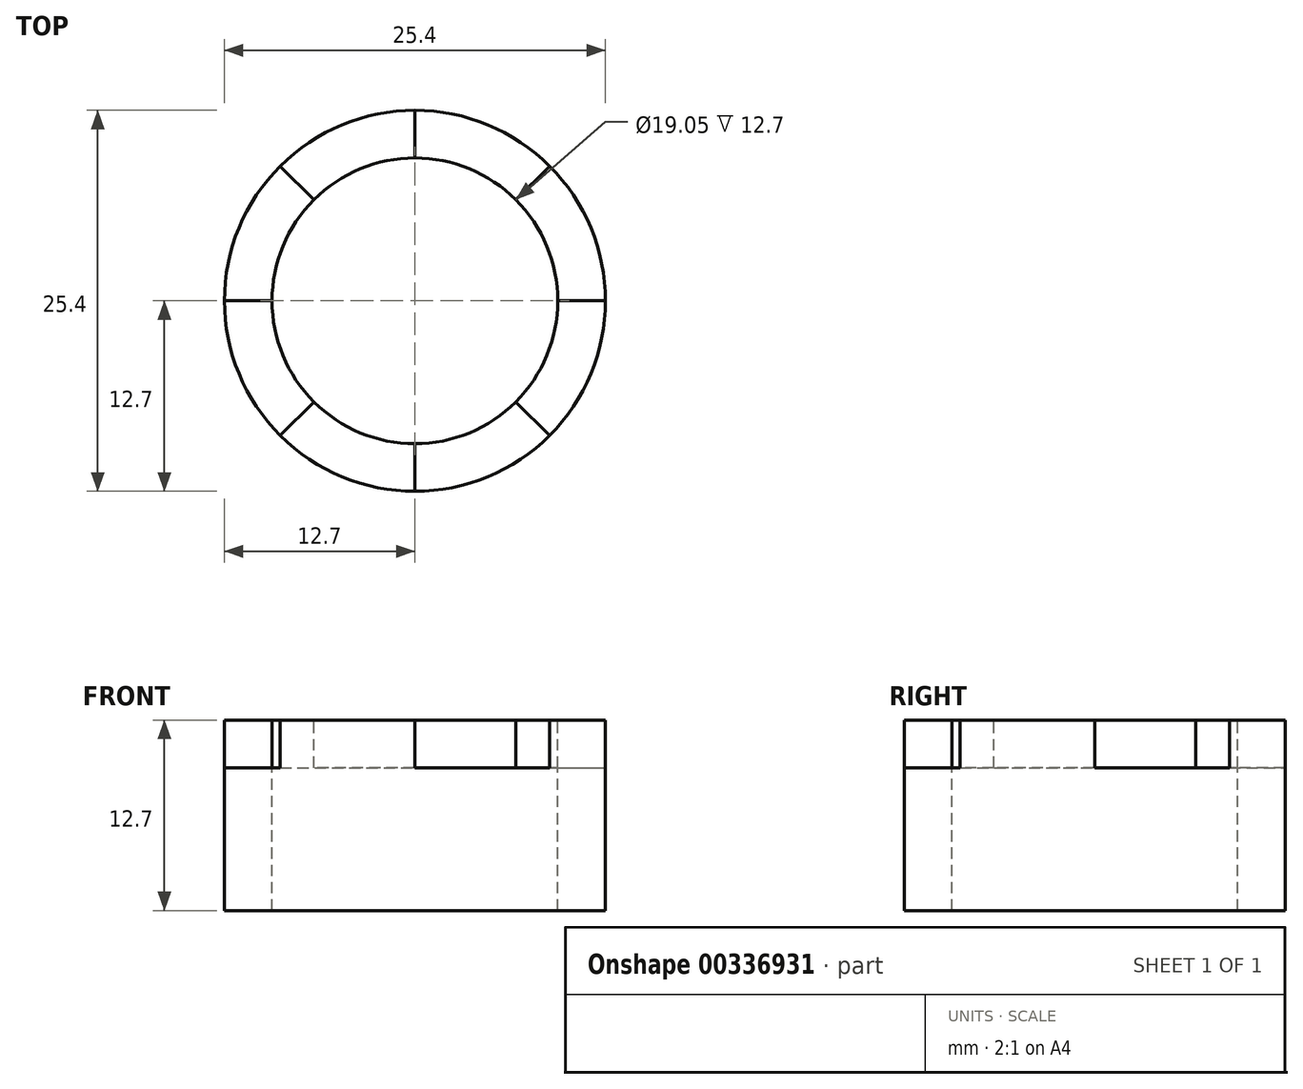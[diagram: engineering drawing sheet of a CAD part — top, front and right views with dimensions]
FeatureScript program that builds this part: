
annotation { "Feature Type Name" : "Feature", "Feature Type Description" : "" }
export const myFeature = defineFeature(function(context is Context, id is Id, definition is map)
    precondition{}
    {
        {
            var Q0;
            Q0=qCreatedBy(makeId("Front.planeOp"),FACE);
            var sketch = newSketch(context, id + "F0", { "sketchPlane" : qUnion([Q0])});
            skLineSegment(sketch, "E0.bottom", {"start": v(25.4, 12.7) * mm, "end": v(0, 12.7) * mm});
            skLineSegment(sketch, "E0.top", {"start": v(25.4, 0) * mm, "end": v(0, 0) * mm});
            skLineSegment(sketch, "E0.left", {"start": v(25.4, 12.7) * mm, "end": v(25.4, 0) * mm});
            skLineSegment(sketch, "E0.right", {"start": v(0, 12.7) * mm, "end": v(0, 0) * mm});
            skLineSegment(sketch, "E1", {"start": v(5.08, 12.7) * mm, "end": v(5.08, 9.52) * mm});
            skLineSegment(sketch, "E2", {"start": v(5.08, 9.52) * mm, "end": v(10.16, 9.52) * mm});
            skLineSegment(sketch, "E3", {"start": v(10.16, 9.52) * mm, "end": v(10.16, 12.7) * mm});
            skLineSegment(sketch, "E4", {"start": v(10.16, 12.7) * mm, "end": v(15.24, 12.7) * mm});
            skLineSegment(sketch, "E5", {"start": v(15.24, 12.7) * mm, "end": v(15.24, 9.52) * mm});
            skLineSegment(sketch, "E6", {"start": v(15.24, 9.52) * mm, "end": v(20.32, 9.52) * mm});
            skLineSegment(sketch, "E7", {"start": v(20.32, 9.53) * mm, "end": v(20.32, 12.7) * mm});
            skSolve(sketch);
        }
        {
            var Q0;
            Q0 = qSketchRegion(id + "F0", true);
            extrude(context, id + "F1", {"entities" : qUnion([Q0]), "depth" : 25.4 * mm});
        }
        {
            var Q0;
            Q0=makeQuery(id+"F1.opExtrude","CAP_EDGE",EDGE,{"disambiguationData":[OSD([sQuery(id+"F0.wireOp",EDGE,"E0.right")])],"isStart":false});
            var Q1;
            Q1=makeQuery(id+"F1.opExtrude","CAP_EDGE",EDGE,{"disambiguationData":[OSD([sQuery(id+"F0.wireOp",EDGE,"E0.left")])],"isStart":false});
            var Q2;
            Q2=makeQuery(id+"F1.opExtrude","CAP_EDGE",EDGE,{"disambiguationData":[OSD([sQuery(id+"F0.wireOp",EDGE,"E0.left")])],"isStart":true});
            var Q3;
            Q3=makeQuery(id+"F1.opExtrude","CAP_EDGE",EDGE,{"disambiguationData":[OSD([sQuery(id+"F0.wireOp",EDGE,"E0.right")])],"isStart":true});
            fillet(context, id + "F2", {"entities" : qUnion([Q0, Q1, Q2, Q3]), "radius" : 12.7 * mm, "tangentPropagation" : true, "allowEdgeOverflow" : false});
        }
        {
            var Q0;
            Q0=makeQuery(id+"F1.opExtrude","SWEPT_FACE",FACE,{"disambiguationData":[OSD([sQuery(id+"F0.wireOp",EDGE,"E0.bottom")])]});
            var sketch = newSketch(context, id + "F3", { "sketchPlane" : qUnion([Q0])});
            skCircle(sketch, "E8", {"center": v(12.7, -12.7) * mm, "radius": 9.53 * mm});
            skSolve(sketch);
        }
        {
            var Q0;
            Q0=makeQuery(id+"F3.imprint","IMPRINT",FACE,{"disambiguationData":[TD([[makeQuery(id+"F3.imprint","IMPRINT",EDGE,{"derivedFrom":sQuery(id+"F3.wireOp",EDGE,"E8")}),1.0]])]});
            extrude(context, id + "F4", {"entities" : qUnion([Q0]), "operationType" : NewBodyOperationType.REMOVE, "endBound" : BoundingType.THROUGH_ALL, "oppositeDirection" : true, "depth" : 25.4 * mm});
        }
        {
            var Q0;
            Q0=makeQuery(id+"F1.opExtrude","SWEPT_FACE",FACE,{"disambiguationData":[OSD([sQuery(id+"F0.wireOp",EDGE,"E0.bottom"),sQuery(id+"F0.wireOp",EDGE,"E4")])]});
            var sketch = newSketch(context, id + "F5", { "sketchPlane" : qUnion([Q0])});
            skLineSegment(sketch, "E9", {"start": v(0, -12.7) * mm, "end": v(3.18, -12.7) * mm});
            skLineSegment(sketch, "E10", {"start": v(12.7, 0) * mm, "end": v(12.7, -3.18) * mm});
            skLineSegment(sketch, "E11", {"start": v(0, 0) * mm, "end": v(5.96, -5.96) * mm});
            skLineSegment(sketch, "E12", {"start": v(19.44, -5.96) * mm, "end": v(21.68, -3.72) * mm});
            skLineSegment(sketch, "E13", {"start": v(5.96, -19.44) * mm, "end": v(3.72, -21.68) * mm});
            skLineSegment(sketch, "E14", {"start": v(19.44, -19.44) * mm, "end": v(21.68, -21.68) * mm});
            skCircle(sketch, "E15", {"center": v(12.7, -12.7) * mm, "radius": 9.53 * mm});
            skLineSegment(sketch, "E16.trimOffspring", {"start": v(12.7, -22.23) * mm, "end": v(12.7, -25.4) * mm});
            skLineSegment(sketch, "E17.trimOffspring", {"start": v(22.23, -12.7) * mm, "end": v(25.4, -12.7) * mm});
            skSolve(sketch);
        }
        {
            var Q0;
            Q0 = qSketchRegion(id + "F5", true);
            var Q1;
            {var subQ0=sQuery(id+"F5.wireOp",EDGE,"E10");Q1=makeQuery(id+"F5.imprint","IMPRINT",FACE,{"disambiguationData":[TD([[makeQuery(id+"F5.imprint","IMPRINT",EDGE,{"derivedFrom":subQ0}),-1.0]])]});}
            var Q2;
            {var subQ0=sQuery(id+"F5.wireOp",EDGE,"E12");Q2=makeQuery(id+"F5.imprint","IMPRINT",FACE,{"disambiguationData":[TD([[makeQuery(id+"F5.imprint","IMPRINT",EDGE,{"derivedFrom":subQ0}),-1.0]])]});}
            var Q3;
            {var subQ0=sQuery(id+"F5.wireOp",EDGE,"E9");Q3=makeQuery(id+"F5.imprint","IMPRINT",FACE,{"disambiguationData":[TD([[makeQuery(id+"F5.imprint","IMPRINT",EDGE,{"derivedFrom":subQ0}),-1.0]])]});}
            var Q4;
            {var subQ0=sQuery(id+"F5.wireOp",EDGE,"E14");Q4=makeQuery(id+"F5.imprint","IMPRINT",FACE,{"disambiguationData":[TD([[makeQuery(id+"F5.imprint","IMPRINT",EDGE,{"derivedFrom":subQ0}),-1.0]])]});}
            extrude(context, id + "F6", {"entities" : qUnion([Q0, Q1, Q2, Q3, Q4]), "operationType" : NewBodyOperationType.REMOVE, "oppositeDirection" : true, "depth" : 3.17 * mm});
        }
    });
